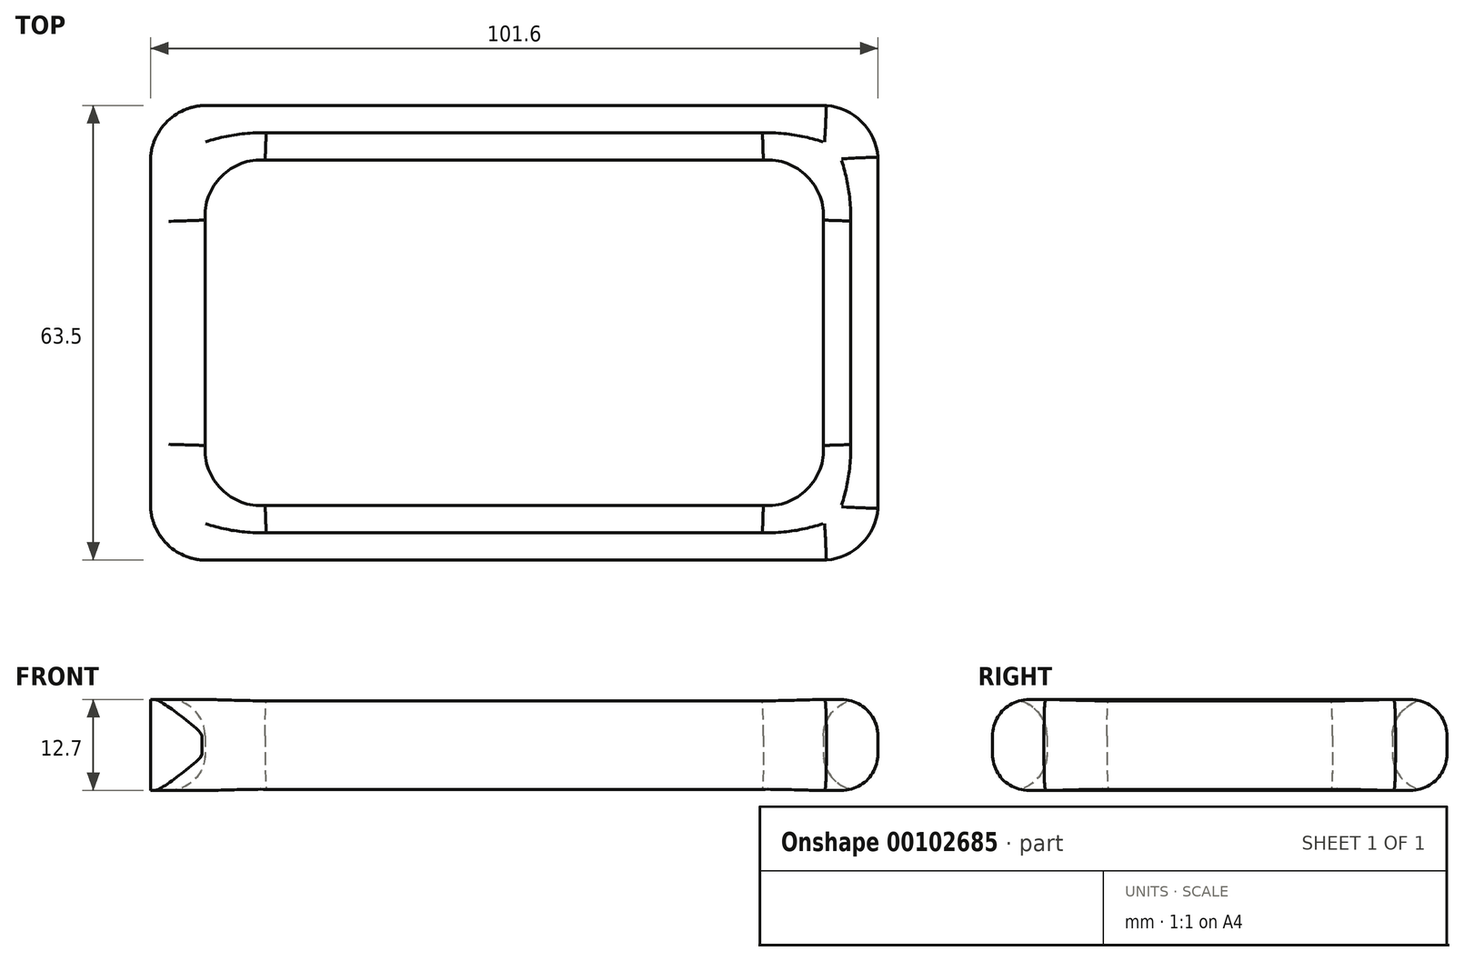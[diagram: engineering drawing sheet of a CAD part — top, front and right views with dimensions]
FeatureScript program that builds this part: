
annotation { "Feature Type Name" : "Feature", "Feature Type Description" : "" }
export const myFeature = defineFeature(function(context is Context, id is Id, definition is map)
    precondition{}
    {
        {
            var Q0;
            Q0=qCreatedBy(makeId("Top.planeOp"),FACE);
            var sketch = newSketch(context, id + "F0", { "sketchPlane" : qUnion([Q0])});
            skLineSegment(sketch, "E0.bottom", {"start": v(-58.11, 31.9) * mm, "end": v(43.49, 31.9) * mm});
            skLineSegment(sketch, "E0.top", {"start": v(-58.11, -31.6) * mm, "end": v(43.49, -31.6) * mm});
            skLineSegment(sketch, "E0.left", {"start": v(-58.11, 31.9) * mm, "end": v(-58.11, -31.6) * mm});
            skLineSegment(sketch, "E0.right", {"start": v(43.49, 31.9) * mm, "end": v(43.49, -31.6) * mm});
            skLineSegment(sketch, "E1.bottom", {"start": v(-50.5, 24.29) * mm, "end": v(35.87, 24.29) * mm});
            skLineSegment(sketch, "E1.top", {"start": v(-50.5, -23.97) * mm, "end": v(35.87, -23.97) * mm});
            skLineSegment(sketch, "E1.left", {"start": v(-50.5, 24.29) * mm, "end": v(-50.5, -23.97) * mm});
            skLineSegment(sketch, "E1.right", {"start": v(35.87, 24.29) * mm, "end": v(35.87, -23.97) * mm});
            skLineSegment(sketch, "E2", {"start": v(-50.5, 26.8) * mm, "end": v(-42.1, 26.8) * mm});
            skLineSegment(sketch, "E3", {"start": v(-53.12, 24.29) * mm, "end": v(-53.12, 15.9) * mm});
            skArc(sketch, "E4", {"start": v(-42.1, 24.29) * mm, "mid": v(-48.23, 22.02) * mm, "end": v(-50.5, 15.9) * mm});
            skLineSegment(sketch, "E5", {"start": v(35.87, 26.87) * mm, "end": v(27.49, 26.87) * mm});
            skLineSegment(sketch, "E6", {"start": v(63.88, 24.29) * mm, "end": v(63.88, 15.9) * mm});
            skArc(sketch, "E7", {"start": v(35.87, 15.9) * mm, "mid": v(33.6, 22.02) * mm, "end": v(27.49, 24.29) * mm});
            skLineSegment(sketch, "E8", {"start": v(-52.88, -23.97) * mm, "end": v(-52.88, -15.6) * mm});
            skLineSegment(sketch, "E9", {"start": v(-50.5, -26.46) * mm, "end": v(-42.1, -26.46) * mm});
            skLineSegment(sketch, "E10", {"start": v(35.87, -25.78) * mm, "end": v(27.49, -25.78) * mm});
            skLineSegment(sketch, "E11", {"start": v(63.34, -23.97) * mm, "end": v(63.34, -15.6) * mm});
            skArc(sketch, "E12", {"start": v(-50.5, -15.6) * mm, "mid": v(-48.23, -21.7) * mm, "end": v(-42.1, -23.97) * mm});
            skArc(sketch, "E13", {"start": v(27.49, -23.97) * mm, "mid": v(33.6, -21.7) * mm, "end": v(35.87, -15.6) * mm});
            skLineSegment(sketch, "E14", {"start": v(43.49, 34.1) * mm, "end": v(35.1, 34.1) * mm});
            skLineSegment(sketch, "E15", {"start": v(45.65, 31.9) * mm, "end": v(45.65, 23.53) * mm});
            skLineSegment(sketch, "E16", {"start": v(-58.11, 34.6) * mm, "end": v(-49.73, 34.6) * mm});
            skLineSegment(sketch, "E17", {"start": v(-61.52, 31.9) * mm, "end": v(-61.52, 23.53) * mm});
            skArc(sketch, "E18", {"start": v(43.49, 23.53) * mm, "mid": v(41.22, 29.64) * mm, "end": v(35.1, 31.9) * mm});
            skArc(sketch, "E19", {"start": v(-49.73, 31.9) * mm, "mid": v(-55.85, 29.64) * mm, "end": v(-58.11, 23.53) * mm});
            skLineSegment(sketch, "E20", {"start": v(-59.6, -31.6) * mm, "end": v(-59.6, -23.21) * mm});
            skLineSegment(sketch, "E21", {"start": v(-58.11, -33.33) * mm, "end": v(-49.73, -33.33) * mm});
            skLineSegment(sketch, "E22", {"start": v(43.49, -33.04) * mm, "end": v(35.1, -33.04) * mm});
            skLineSegment(sketch, "E23", {"start": v(45.07, -31.6) * mm, "end": v(45.07, -23.21) * mm});
            skArc(sketch, "E24", {"start": v(-58.11, -23.21) * mm, "mid": v(-55.85, -29.33) * mm, "end": v(-49.73, -31.6) * mm});
            skArc(sketch, "E25", {"start": v(35.1, -31.6) * mm, "mid": v(41.22, -29.33) * mm, "end": v(43.49, -23.21) * mm});
            skSolve(sketch);
        }
        {
            var Q0;
            Q0=makeQuery(id+"F0.imprint","IMPRINT",FACE,{"disambiguationData":[TD([[makeQuery(id+"F0.imprint","IMPRINT",EDGE,{"derivedFrom":sQuery(id+"F0.wireOp",EDGE,"E0.bottom")}),-1.0]])]});
            var Q1;
            {var subQ0=sQuery(id+"F0.wireOp",EDGE,"E1.left");var subQ1=sQuery(id+"F0.wireOp",EDGE,"E1.bottom");var subQ2=makeQuery(id+"F0.imprint","INTERSECT",VERTEX,{"derivedFrom":[subQ1,subQ0]});Q1=makeQuery(id+"F0.imprint","IMPRINT",FACE,{"disambiguationData":[TD([[makeQuery(id+"F0.imprint","IMPRINT",EDGE,{"disambiguationData":[TD([[subQ2,-1.0]])],"derivedFrom":subQ1}),-1.0]])]});}
            var Q2;
            {var subQ0=sQuery(id+"F0.wireOp",EDGE,"E1.right");var subQ1=sQuery(id+"F0.wireOp",EDGE,"E1.bottom");var subQ2=makeQuery(id+"F0.imprint","INTERSECT",VERTEX,{"derivedFrom":[subQ1,subQ0]});Q2=makeQuery(id+"F0.imprint","IMPRINT",FACE,{"disambiguationData":[TD([[makeQuery(id+"F0.imprint","IMPRINT",EDGE,{"disambiguationData":[TD([[subQ2,1.0]])],"derivedFrom":subQ1}),-1.0]])]});}
            var Q3;
            {var subQ0=sQuery(id+"F0.wireOp",EDGE,"E1.right");var subQ1=sQuery(id+"F0.wireOp",EDGE,"E1.top");var subQ2=makeQuery(id+"F0.imprint","INTERSECT",VERTEX,{"derivedFrom":[subQ1,subQ0]});Q3=makeQuery(id+"F0.imprint","IMPRINT",FACE,{"disambiguationData":[TD([[makeQuery(id+"F0.imprint","IMPRINT",EDGE,{"disambiguationData":[TD([[subQ2,1.0]])],"derivedFrom":subQ1}),1.0]])]});}
            var Q4;
            {var subQ0=sQuery(id+"F0.wireOp",EDGE,"E1.left");var subQ1=sQuery(id+"F0.wireOp",EDGE,"E1.top");var subQ2=makeQuery(id+"F0.imprint","INTERSECT",VERTEX,{"derivedFrom":[subQ1,subQ0]});Q4=makeQuery(id+"F0.imprint","IMPRINT",FACE,{"disambiguationData":[TD([[makeQuery(id+"F0.imprint","IMPRINT",EDGE,{"disambiguationData":[TD([[subQ2,-1.0]])],"derivedFrom":subQ1}),1.0]])]});}
            extrude(context, id + "F1", {"entities" : qUnion([Q0, Q1, Q2, Q3, Q4]), "depth" : 12.7 * mm});
        }
        {
            var Q0;
            Q0=makeQuery(id+"F1.opExtrude","CAP_EDGE",EDGE,{"disambiguationData":[OSD([sQuery(id+"F0.wireOp",EDGE,"E0.top")])],"isStart":false});
            var Q1;
            Q1=makeQuery(id+"F1.opExtrude","CAP_EDGE",EDGE,{"disambiguationData":[OSD([sQuery(id+"F0.wireOp",EDGE,"E0.top")])],"isStart":true});
            var Q2;
            Q2=makeQuery(id+"F1.opExtrude","CAP_EDGE",EDGE,{"disambiguationData":[OSD([sQuery(id+"F0.wireOp",EDGE,"E0.right")])],"isStart":false});
            var Q3;
            Q3=makeQuery(id+"F1.opExtrude","CAP_EDGE",EDGE,{"disambiguationData":[OSD([sQuery(id+"F0.wireOp",EDGE,"E0.right")])],"isStart":true});
            var Q4;
            Q4=makeQuery(id+"F1.opExtrude","CAP_EDGE",EDGE,{"disambiguationData":[OSD([sQuery(id+"F0.wireOp",EDGE,"E0.bottom")])],"isStart":false});
            var Q5;
            Q5=makeQuery(id+"F1.opExtrude","CAP_EDGE",EDGE,{"disambiguationData":[OSD([sQuery(id+"F0.wireOp",EDGE,"E0.bottom")])],"isStart":true});
            fillet(context, id + "F2", {"entities" : qUnion([Q0, Q1, Q2, Q3, Q4, Q5]), "radius" : 5.08 * mm, "tangentPropagation" : true, "allowEdgeOverflow" : false});
        }
        {
            var Q0;
            Q0=makeQuery(id+"F1.opExtrude","CAP_EDGE",EDGE,{"disambiguationData":[OSD([sQuery(id+"F0.wireOp",EDGE,"E4")])],"isStart":false});
            var Q1;
            Q1=makeQuery(id+"F1.opExtrude","CAP_EDGE",EDGE,{"disambiguationData":[OSD([sQuery(id+"F0.wireOp",EDGE,"E7")])],"isStart":false});
            var Q2;
            Q2=makeQuery(id+"F1.opExtrude","CAP_EDGE",EDGE,{"disambiguationData":[OSD([sQuery(id+"F0.wireOp",EDGE,"E7")])],"isStart":true});
            var Q3;
            Q3=makeQuery(id+"F1.opExtrude","CAP_EDGE",EDGE,{"disambiguationData":[OSD([sQuery(id+"F0.wireOp",EDGE,"E4")])],"isStart":true});
            var Q4;
            Q4=makeQuery(id+"F1.opExtrude","CAP_EDGE",EDGE,{"disambiguationData":[OSD([sQuery(id+"F0.wireOp",EDGE,"E1.bottom")])],"isStart":true});
            var Q5;
            Q5=makeQuery(id+"F1.opExtrude","CAP_EDGE",EDGE,{"disambiguationData":[OSD([sQuery(id+"F0.wireOp",EDGE,"E1.bottom")])],"isStart":false});
            var Q6;
            Q6=makeQuery(id+"F1.opExtrude","CAP_EDGE",EDGE,{"disambiguationData":[OSD([sQuery(id+"F0.wireOp",EDGE,"E12")])],"isStart":false});
            var Q7;
            Q7=makeQuery(id+"F1.opExtrude","CAP_EDGE",EDGE,{"disambiguationData":[OSD([sQuery(id+"F0.wireOp",EDGE,"E1.left")])],"isStart":false});
            var Q8;
            Q8=makeQuery(id+"F1.opExtrude","CAP_EDGE",EDGE,{"disambiguationData":[OSD([sQuery(id+"F0.wireOp",EDGE,"E12")])],"isStart":true});
            var Q9;
            Q9=makeQuery(id+"F1.opExtrude","CAP_EDGE",EDGE,{"disambiguationData":[OSD([sQuery(id+"F0.wireOp",EDGE,"E1.left")])],"isStart":true});
            var Q10;
            Q10=makeQuery(id+"F1.opExtrude","CAP_EDGE",EDGE,{"disambiguationData":[OSD([sQuery(id+"F0.wireOp",EDGE,"E13")])],"isStart":false});
            var Q11;
            Q11=makeQuery(id+"F1.opExtrude","CAP_EDGE",EDGE,{"disambiguationData":[OSD([sQuery(id+"F0.wireOp",EDGE,"E13")])],"isStart":true});
            var Q12;
            Q12=makeQuery(id+"F1.opExtrude","CAP_EDGE",EDGE,{"disambiguationData":[OSD([sQuery(id+"F0.wireOp",EDGE,"E1.right")])],"isStart":true});
            var Q13;
            Q13=makeQuery(id+"F1.opExtrude","CAP_EDGE",EDGE,{"disambiguationData":[OSD([sQuery(id+"F0.wireOp",EDGE,"E1.right")])],"isStart":false});
            var Q14;
            Q14=makeQuery(id+"F1.opExtrude","CAP_EDGE",EDGE,{"disambiguationData":[OSD([sQuery(id+"F0.wireOp",EDGE,"E1.top")])],"isStart":false});
            var Q15;
            Q15=makeQuery(id+"F1.opExtrude","CAP_EDGE",EDGE,{"disambiguationData":[OSD([sQuery(id+"F0.wireOp",EDGE,"E1.top")])],"isStart":true});
            fillet(context, id + "F3", {"entities" : qUnion([Q0, Q1, Q2, Q3, Q4, Q5, Q6, Q7, Q8, Q9, Q10, Q11, Q12, Q13, Q14, Q15]), "radius" : 5.08 * mm, "tangentPropagation" : true, "allowEdgeOverflow" : false});
        }
    });
